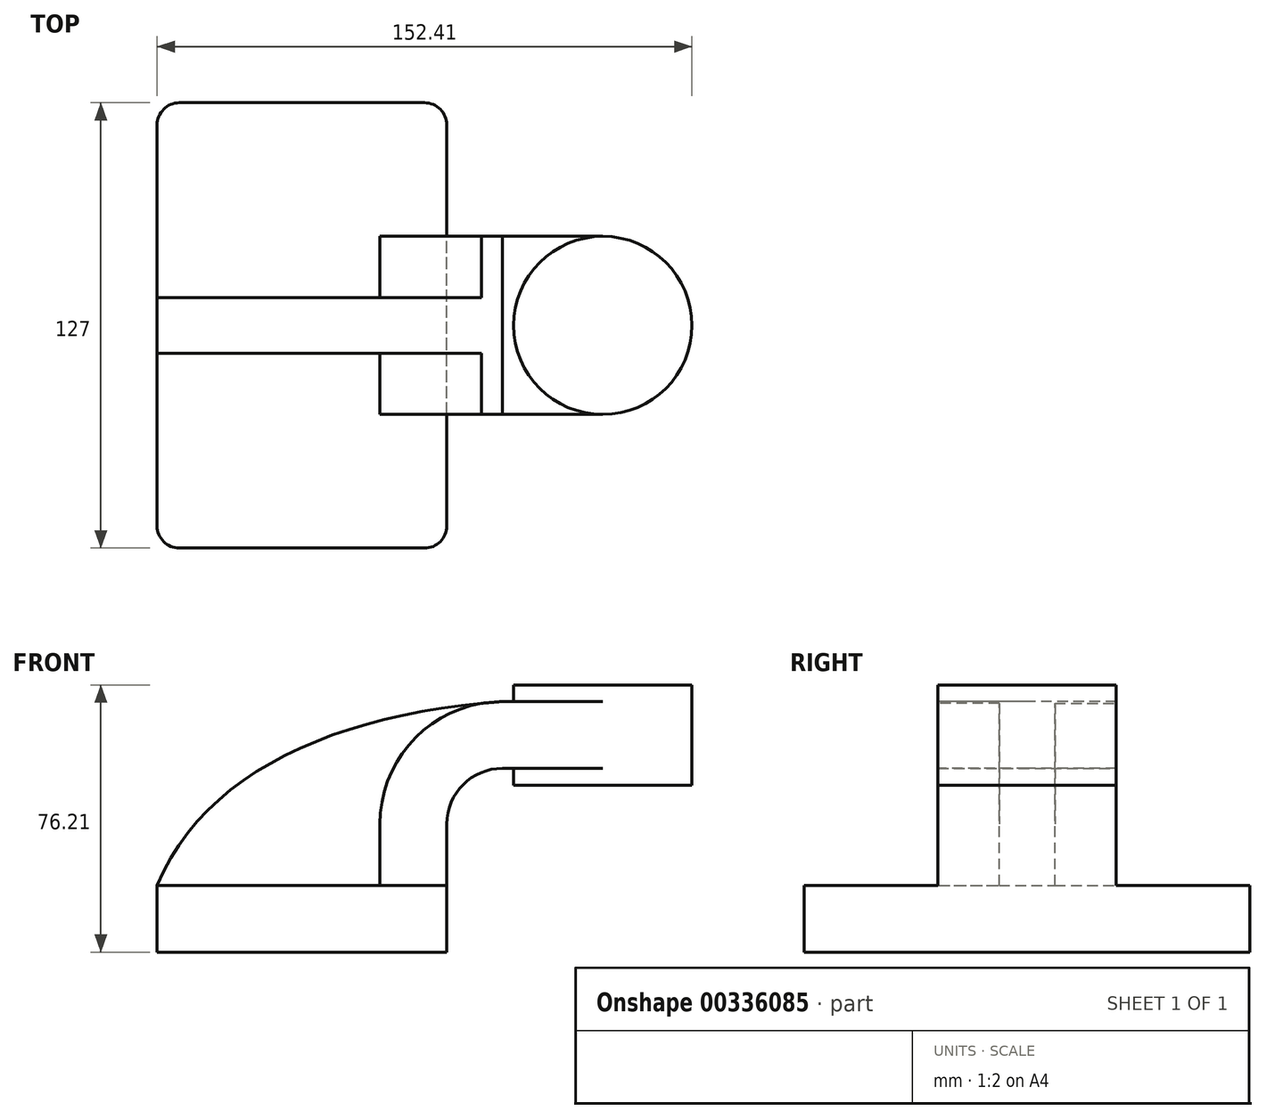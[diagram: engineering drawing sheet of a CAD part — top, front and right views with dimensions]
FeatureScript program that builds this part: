
annotation { "Feature Type Name" : "Feature", "Feature Type Description" : "" }
export const myFeature = defineFeature(function(context is Context, id is Id, definition is map)
    precondition{}
    {
        {
            var Q0;
            Q0=qCreatedBy(makeId("Front.planeOp"),FACE);
            var sketch = newSketch(context, id + "F0", { "sketchPlane" : qUnion([Q0])});
            skLineSegment(sketch, "E0.bottom", {"start": v(-41.28, 9.52) * mm, "end": v(41.27, 9.53) * mm});
            skLineSegment(sketch, "E0.top", {"start": v(-41.28, -9.53) * mm, "end": v(41.28, -9.53) * mm});
            skLineSegment(sketch, "E0.left", {"start": v(-41.28, 9.52) * mm, "end": v(-41.28, -9.53) * mm});
            skLineSegment(sketch, "E0.right", {"start": v(41.27, 9.53) * mm, "end": v(41.28, -9.52) * mm});
            skPoint(sketch, "E0.middle", {"position": v(0, 0) * mm});
            skLineSegment(sketch, "E1.bottom", {"start": v(60.32, 66.68) * mm, "end": v(111.12, 66.68) * mm});
            skLineSegment(sketch, "E1.top", {"start": v(60.32, 38.1) * mm, "end": v(111.12, 38.1) * mm});
            skLineSegment(sketch, "E1.left", {"start": v(60.32, 66.68) * mm, "end": v(60.32, 38.1) * mm});
            skLineSegment(sketch, "E1.right", {"start": v(111.12, 66.68) * mm, "end": v(111.12, 38.1) * mm});
            skPoint(sketch, "E1.middle", {"position": v(85.72, 52.39) * mm});
            skLineSegment(sketch, "E2", {"start": v(41.27, 9.53) * mm, "end": v(41.27, 27) * mm});
            skArc(sketch, "E3", {"start": v(41.27, 27) * mm, "mid": v(45.92, 38.23) * mm, "end": v(57.15, 42.88) * mm});
            skArc(sketch, "E4.1", {"start": v(22.22, 27) * mm, "mid": v(32.45, 51.7) * mm, "end": v(57.15, 61.93) * mm});
            skLineSegment(sketch, "E4.2", {"start": v(22.22, 9.53) * mm, "end": v(22.22, 27) * mm});
            skLineSegment(sketch, "E5", {"start": v(85.72, 38.1) * mm, "end": v(85.72, 66.68) * mm});
            skLineSegment(sketch, "E6", {"start": v(57.15, 61.93) * mm, "end": v(85.72, 61.93) * mm});
            skLineSegment(sketch, "E7", {"start": v(57.15, 42.88) * mm, "end": v(85.72, 42.88) * mm});
            skFitSpline(sketch, "E8", {"points": [v(-41.28, 9.52) * mm, v(57.15, 61.93) * mm], "startDerivative": vector(40.85, 97.17) * mm, "endDerivative": vector(142.75, 10.5) * mm});
            skSolve(sketch);
        }
        {
            var Q0;
            Q0=makeQuery(id+"F0.imprint","IMPRINT",FACE,{"disambiguationData":[TD([[makeQuery(id+"F0.imprint","IMPRINT",EDGE,{"derivedFrom":sQuery(id+"F0.wireOp",EDGE,"E0.top")}),1.0]])]});
            extrude(context, id + "F1", {"entities" : qUnion([Q0]), "endBound" : BoundingType.SYMMETRIC, "depth" : 127 * mm});
        }
        {
            var Q0;
            {var subQ1=sQuery(id+"F0.wireOp",EDGE,"E2");Q0=makeQuery(id+"F0.imprint","IMPRINT",FACE,{"disambiguationData":[TD([[makeQuery(id+"F0.imprint","IMPRINT",EDGE,{"derivedFrom":subQ1}),1.0]])]});}
            extrude(context, id + "F2", {"entities" : qUnion([Q0]), "operationType" : NewBodyOperationType.ADD, "endBound" : BoundingType.SYMMETRIC, "depth" : 50.8 * mm});
        }
        {
            var Q0;
            {var subQ0=sQuery(id+"F0.wireOp",EDGE,"E6");var subQ1=sQuery(id+"F0.wireOp",EDGE,"E1.left");var subQ2=makeQuery(id+"F0.imprint","INTERSECT",VERTEX,{"derivedFrom":[subQ1,subQ0]});Q0=makeQuery(id+"F0.imprint","IMPRINT",FACE,{"disambiguationData":[TD([[makeQuery(id+"F0.imprint","IMPRINT",EDGE,{"disambiguationData":[TD([[subQ2,-1.0]])],"derivedFrom":subQ1}),1.0]])]});}
            extrude(context, id + "F3", {"entities" : qUnion([Q0]), "operationType" : NewBodyOperationType.ADD, "endBound" : BoundingType.SYMMETRIC, "depth" : 50.8 * mm});
        }
        {
            var Q0;
            {var subQ0=sQuery(id+"F0.wireOp",EDGE,"E1.right");Q0=makeQuery(id+"F0.imprint","IMPRINT",FACE,{"disambiguationData":[TD([[makeQuery(id+"F0.imprint","IMPRINT",EDGE,{"derivedFrom":subQ0}),-1.0]])]});}
            var Q1;
            Q1=sQuery(id+"F0.wireOp",EDGE,"E5");
            revolve(context, id + "F4", {"operationType" : NewBodyOperationType.ADD, "entities" : qUnion([Q0]), "axis" : qUnion([Q1]), "revolveType" : RevolveType.FULL});
        }
        {
            var Q0;
            {var subQ3=sQuery(id+"F0.wireOp",EDGE,"E4.2");Q0=makeQuery(id+"F0.imprint","IMPRINT",FACE,{"disambiguationData":[TD([[makeQuery(id+"F0.imprint","IMPRINT",EDGE,{"derivedFrom":subQ3}),1.0]])]});}
            extrude(context, id + "F5", {"entities" : qUnion([Q0]), "operationType" : NewBodyOperationType.ADD, "endBound" : BoundingType.SYMMETRIC, "depth" : 15.88 * mm});
        }
        {
            var Q0;
            Q0=makeQuery(id+"F1.opExtrude","CAP_EDGE",EDGE,{"disambiguationData":[OSD([sQuery(id+"F0.wireOp",EDGE,"E0.left")])],"isStart":false});
            var Q1;
            Q1=makeQuery(id+"F1.opExtrude","CAP_EDGE",EDGE,{"disambiguationData":[OSD([sQuery(id+"F0.wireOp",EDGE,"E0.right")])],"isStart":false});
            var Q2;
            Q2=makeQuery(id+"F1.opExtrude","CAP_EDGE",EDGE,{"disambiguationData":[OSD([sQuery(id+"F0.wireOp",EDGE,"E0.right")])],"isStart":true});
            var Q3;
            Q3=makeQuery(id+"F1.opExtrude","CAP_EDGE",EDGE,{"disambiguationData":[OSD([sQuery(id+"F0.wireOp",EDGE,"E0.left")])],"isStart":true});
            fillet(context, id + "F6", {"entities" : qUnion([Q0, Q1, Q2, Q3]), "radius" : 6.35 * mm, "tangentPropagation" : true, "allowEdgeOverflow" : false});
        }
    });
